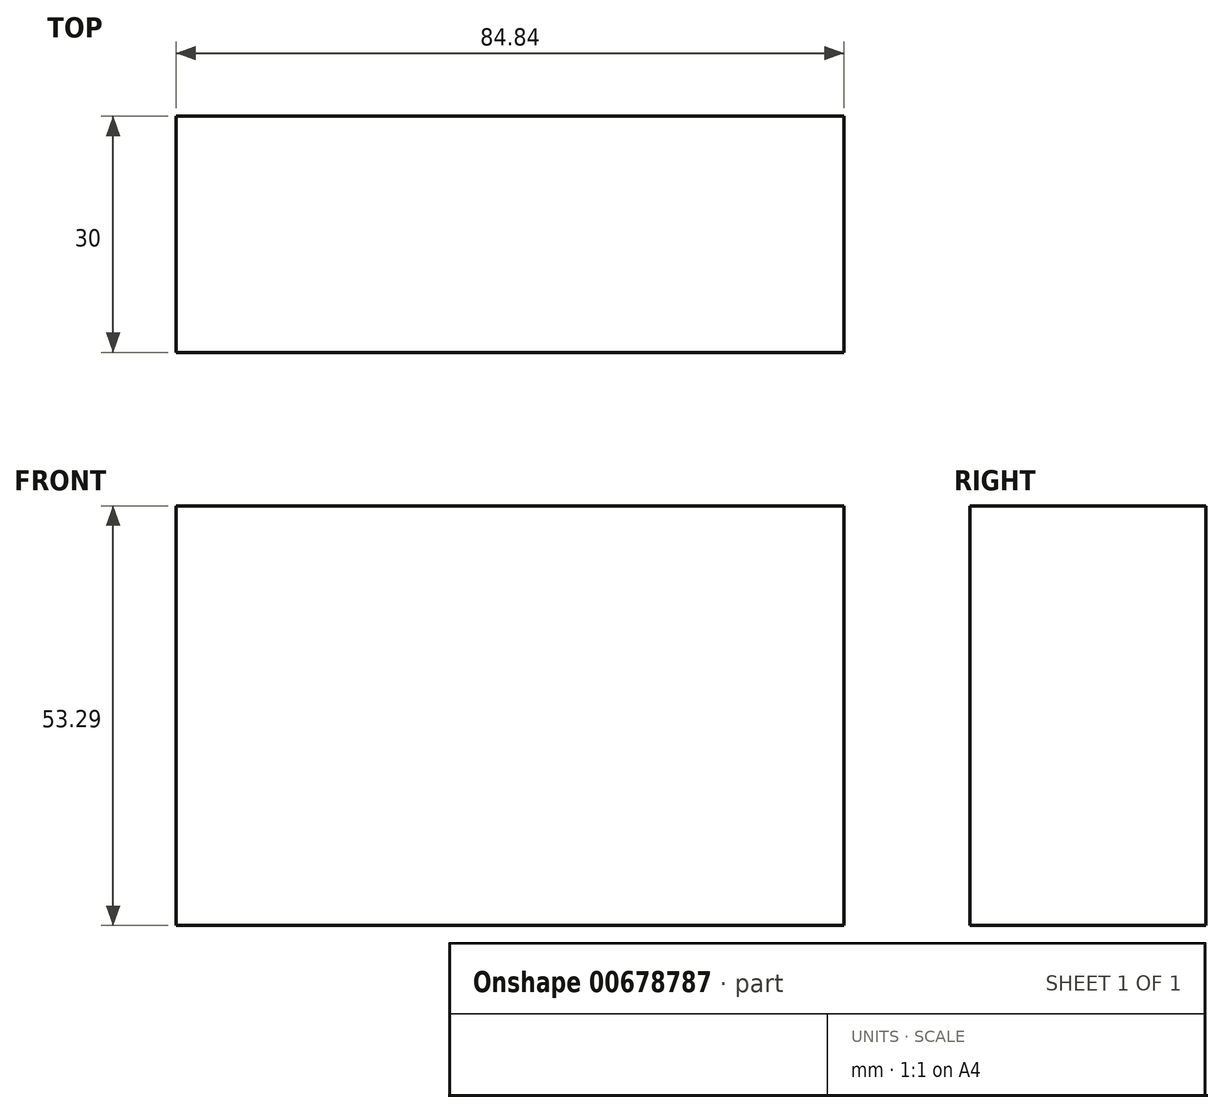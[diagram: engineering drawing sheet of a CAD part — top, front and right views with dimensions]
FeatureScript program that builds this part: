
annotation { "Feature Type Name" : "Feature", "Feature Type Description" : "" }
export const myFeature = defineFeature(function(context is Context, id is Id, definition is map)
    precondition{}
    {
        {
            var Q0;
            Q0=qCreatedBy(makeId("Front.planeOp"),FACE);
            var sketch = newSketch(context, id + "F0", { "sketchPlane" : qUnion([Q0])});
            skLineSegment(sketch, "E0.bottom", {"start": v(39.9, 0) * mm, "end": v(-44.94, 0) * mm});
            skLineSegment(sketch, "E0.top", {"start": v(39.9, -53.3) * mm, "end": v(-44.94, -53.3) * mm});
            skLineSegment(sketch, "E0.left", {"start": v(39.9, 0) * mm, "end": v(39.9, -53.3) * mm});
            skLineSegment(sketch, "E0.right", {"start": v(-44.94, 0) * mm, "end": v(-44.94, -53.3) * mm});
            skSolve(sketch);
        }
        {
            var Q0;
            Q0=makeQuery(id+"F0.imprint","IMPRINT",FACE,{"disambiguationData":[TD([[makeQuery(id+"F0.imprint","IMPRINT",EDGE,{"derivedFrom":sQuery(id+"F0.wireOp",EDGE,"E0.bottom")}),1.0]])]});
            extrude(context, id + "F1", {"entities" : qUnion([Q0]), "depth" : 30 * mm, "offsetDistance" : 25 * mm});
        }
    });
